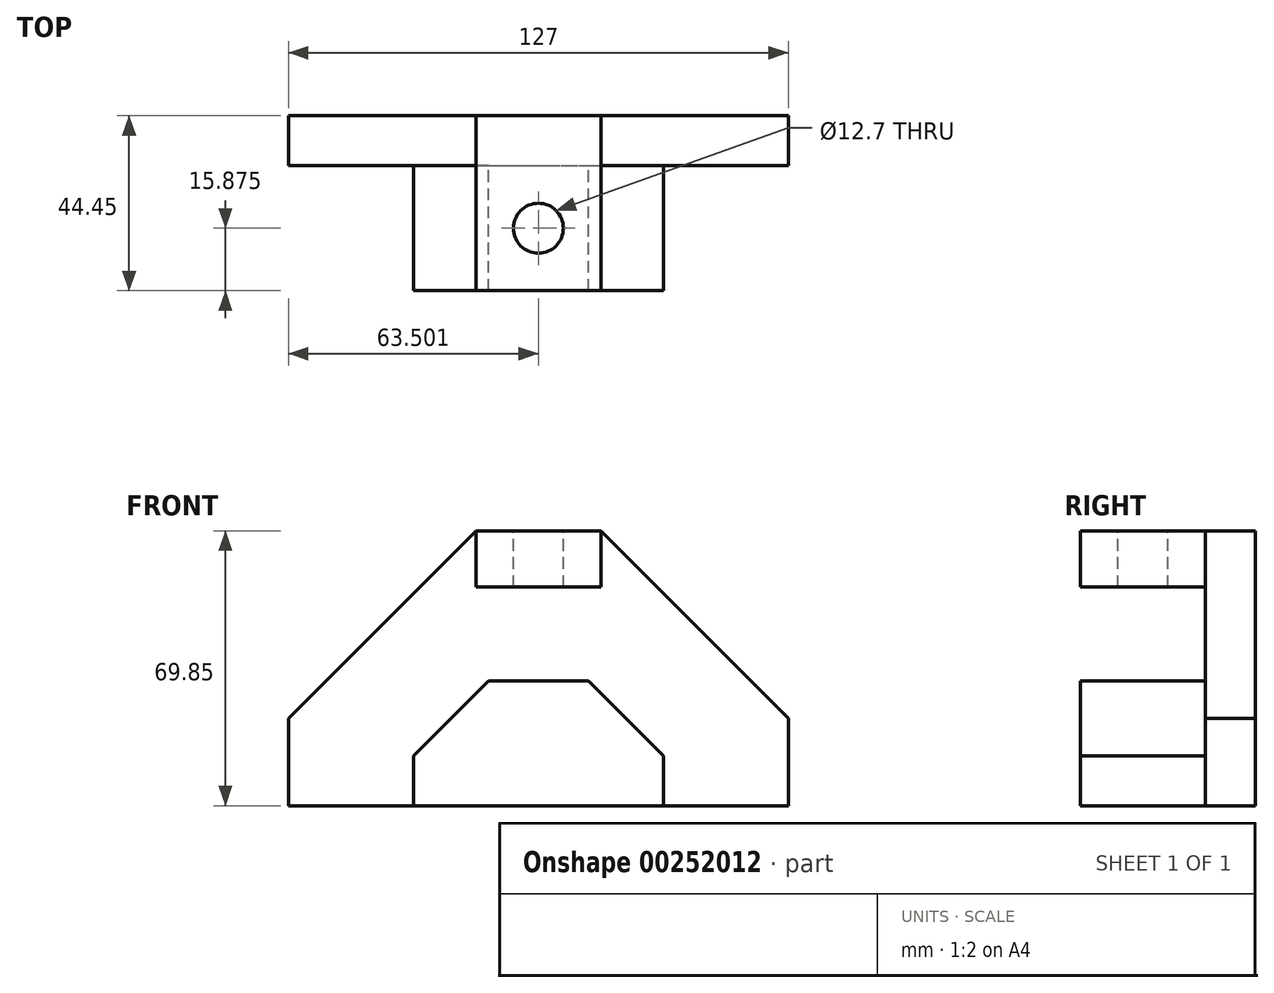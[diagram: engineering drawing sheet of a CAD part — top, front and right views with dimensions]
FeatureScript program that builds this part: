
annotation { "Feature Type Name" : "Feature", "Feature Type Description" : "" }
export const myFeature = defineFeature(function(context is Context, id is Id, definition is map)
    precondition{}
    {
        {
            var Q0;
            Q0=qCreatedBy(makeId("Front.planeOp"),FACE);
            var sketch = newSketch(context, id + "F0", { "sketchPlane" : qUnion([Q0])});
            skLineSegment(sketch, "E0.bottom", {"start": v(-74.19, -11.72) * mm, "end": v(52.81, -11.72) * mm});
            skLineSegment(sketch, "E0.top", {"start": v(-74.19, 58.13) * mm, "end": v(52.81, 58.13) * mm});
            skLineSegment(sketch, "E0.left", {"start": v(-74.19, -11.72) * mm, "end": v(-74.19, 58.13) * mm});
            skLineSegment(sketch, "E0.right", {"start": v(52.81, -11.72) * mm, "end": v(52.81, 58.13) * mm});
            skLineSegment(sketch, "E1", {"start": v(5.19, 58.13) * mm, "end": v(52.81, 10.5) * mm});
            skLineSegment(sketch, "E2", {"start": v(-26.56, 58.13) * mm, "end": v(-74.19, 10.5) * mm});
            skSolve(sketch);
        }
        {
            var Q0;
            {var subQ1=sQuery(id+"F0.wireOp",EDGE,"E0.bottom");Q0=makeQuery(id+"F0.imprint","IMPRINT",FACE,{"disambiguationData":[TD([[makeQuery(id+"F0.imprint","IMPRINT",EDGE,{"derivedFrom":subQ1}),1.0]])]});}
            extrude(context, id + "F1", {"entities" : qUnion([Q0]), "depth" : 12.7 * mm});
        }
        {
            var Q0;
            Q0=makeQuery(id+"F1.opExtrude","CAP_FACE",FACE,{"disambiguationData":[OSD([sQuery(id+"F0.wireOp",EDGE,"E0.bottom"),sQuery(id+"F0.wireOp",EDGE,"E0.top"),sQuery(id+"F0.wireOp",EDGE,"E0.left"),sQuery(id+"F0.wireOp",EDGE,"E0.right"),sQuery(id+"F0.wireOp",EDGE,"E1"),sQuery(id+"F0.wireOp",EDGE,"E2")])],"isStart":false});
            var sketch = newSketch(context, id + "F2", { "sketchPlane" : qUnion([Q0])});
            skLineSegment(sketch, "E3.bottom", {"start": v(-42.44, -11.72) * mm, "end": v(21.06, -11.72) * mm});
            skLineSegment(sketch, "E3.top", {"start": v(-42.44, 20.03) * mm, "end": v(21.06, 20.03) * mm});
            skLineSegment(sketch, "E3.left", {"start": v(-42.44, -11.72) * mm, "end": v(-42.44, 20.03) * mm});
            skLineSegment(sketch, "E3.right", {"start": v(21.06, -11.72) * mm, "end": v(21.06, 20.03) * mm});
            skPoint(sketch, "E3.middle", {"position": v(-10.69, 4.16) * mm});
            skLineSegment(sketch, "E4", {"start": v(2.01, 20.03) * mm, "end": v(21.06, 0.98) * mm});
            skLineSegment(sketch, "E5", {"start": v(-23.39, 20.03) * mm, "end": v(-42.44, 0.98) * mm});
            skSolve(sketch);
        }
        {
            var Q0;
            {var subQ1=sQuery(id+"F2.wireOp",EDGE,"E3.bottom");Q0=makeQuery(id+"F2.imprint","IMPRINT",FACE,{"disambiguationData":[TD([[makeQuery(id+"F2.imprint","IMPRINT",EDGE,{"derivedFrom":subQ1}),1.0]])]});}
            extrude(context, id + "F3", {"entities" : qUnion([Q0]), "operationType" : NewBodyOperationType.ADD, "depth" : 31.75 * mm});
        }
        {
            var Q0;
            Q0=makeQuery(id+"F1.opExtrude","SWEPT_FACE",FACE,{"disambiguationData":[OSD([sQuery(id+"F0.wireOp",EDGE,"E0.top")])]});
            var sketch = newSketch(context, id + "F4", { "sketchPlane" : qUnion([Q0])});
            skLineSegment(sketch, "E6.bottom", {"start": v(-26.56, 0) * mm, "end": v(5.19, 0) * mm});
            skLineSegment(sketch, "E6.top", {"start": v(-26.56, -44.45) * mm, "end": v(5.19, -44.45) * mm});
            skLineSegment(sketch, "E6.left", {"start": v(-26.56, 0) * mm, "end": v(-26.56, -44.45) * mm});
            skLineSegment(sketch, "E6.right", {"start": v(5.19, 0) * mm, "end": v(5.19, -44.45) * mm});
            skSolve(sketch);
        }
        {
            var Q0;
            {var subQ0=sQuery(id+"F4.wireOp",EDGE,"E6.top");Q0=makeQuery(id+"F4.imprint","IMPRINT",FACE,{"disambiguationData":[TD([[makeQuery(id+"F4.imprint","IMPRINT",EDGE,{"derivedFrom":subQ0}),1.0]])]});}
            extrude(context, id + "F5", {"entities" : qUnion([Q0]), "operationType" : NewBodyOperationType.ADD, "oppositeDirection" : true, "depth" : 14.29 * mm});
        }
        {
            var Q0;
            {var subQ0=sQuery(id+"F0.wireOp",EDGE,"E0.top");Q0=makeQuery(id+"F5.boolean.opBoolean","MERGE",FACE,{"derivedFrom":[makeQuery(id+"F1.opExtrude","SWEPT_FACE",FACE,{"disambiguationData":[OSD([subQ0])]}),makeQuery(id+"F5.opExtrude","CAP_FACE",FACE,{"disambiguationData":[OSD([subQ0,sQuery(id+"F4.wireOp",EDGE,"E6.top"),sQuery(id+"F4.wireOp",EDGE,"E6.left"),sQuery(id+"F4.wireOp",EDGE,"E6.right")])],"isStart":true})]});}
            var sketch = newSketch(context, id + "F6", { "sketchPlane" : qUnion([Q0])});
            skCircle(sketch, "E7", {"center": v(-10.69, -28.58) * mm, "radius": 6.35 * mm});
            skPoint(sketch, "E7.centerSnap0", {"position": v(-10.69, -44.45) * mm});
            skSolve(sketch);
        }
        {
            var Q0;
            Q0 = qSketchRegion(id + "F6", true);
            extrude(context, id + "F7", {"entities" : qUnion([Q0]), "operationType" : NewBodyOperationType.REMOVE, "oppositeDirection" : true, "depth" : 25.4 * mm});
        }
    });
